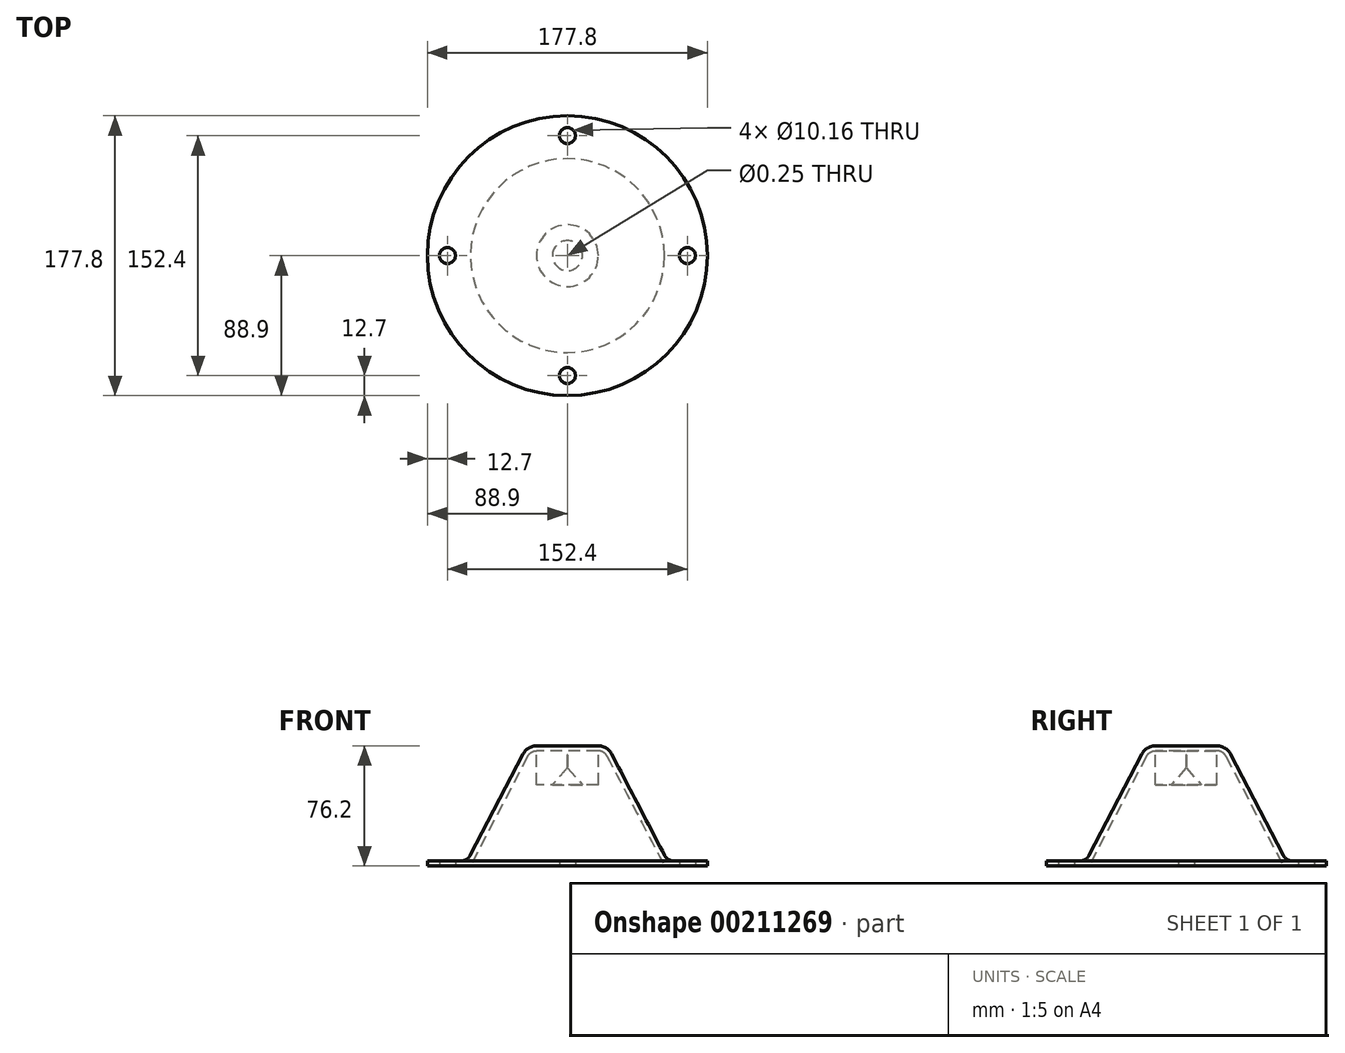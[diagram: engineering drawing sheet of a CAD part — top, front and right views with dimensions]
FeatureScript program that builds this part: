
annotation { "Feature Type Name" : "Feature", "Feature Type Description" : "" }
export const myFeature = defineFeature(function(context is Context, id is Id, definition is map)
    precondition{}
    {
        {
            var Q0;
            Q0=qCreatedBy(makeId("Front.planeOp"),FACE);
            var sketch = newSketch(context, id + "F0", { "sketchPlane" : qUnion([Q0])});
            skLineSegment(sketch, "E0", {"start": v(61.58, 0) * mm, "end": v(88.9, 0) * mm});
            skLineSegment(sketch, "E1", {"start": v(0, 73.03) * mm, "end": v(0, 76.2) * mm});
            skLineSegment(sketch, "E2", {"start": v(88.9, 0) * mm, "end": v(88.9, 3.18) * mm});
            skLineSegment(sketch, "E3", {"start": v(88.9, 3.18) * mm, "end": v(67.35, 3.18) * mm});
            skLineSegment(sketch, "E4", {"start": v(0, 76.2) * mm, "end": v(19.63, 76.2) * mm});
            skLineSegment(sketch, "E5", {"start": v(28.07, 71.08) * mm, "end": v(61.72, 6.59) * mm});
            skLineSegment(sketch, "E6", {"start": v(0, 76.2) * mm, "end": v(0, 73.03) * mm});
            skLineSegment(sketch, "E7", {"start": v(0, 73.03) * mm, "end": v(19.63, 73.03) * mm});
            skLineSegment(sketch, "E8", {"start": v(25.26, 69.61) * mm, "end": v(61.58, 0) * mm});
            skPoint(sketch, "E9.orphan", {"position": v(-148.64, 0) * mm});
            skPoint(sketch, "E10.visualSharp", {"position": v(23.48, 73.03) * mm});
            skArc(sketch, "E10.filletArc", {"start": v(25.26, 69.61) * mm, "mid": v(22.92, 72.1) * mm, "end": v(19.63, 73.03) * mm});
            skPoint(sketch, "E11.visualSharp", {"position": v(63.5, 3.18) * mm});
            skArc(sketch, "E11.filletArc", {"start": v(61.72, 6.59) * mm, "mid": v(64.06, 4.1) * mm, "end": v(67.35, 3.18) * mm});
            skPoint(sketch, "E12.visualSharp", {"position": v(25.4, 76.2) * mm});
            skArc(sketch, "E12.filletArc", {"start": v(28.07, 71.08) * mm, "mid": v(24.56, 74.82) * mm, "end": v(19.63, 76.2) * mm});
            skLineSegment(sketch, "E13", {"start": v(0, 54.17) * mm, "end": v(0, 16.24) * mm});
            skSolve(sketch);
        }
        {
            var Q0;
            Q0 = qSketchRegion(id + "F0", true);
            var Q1;
            Q1=sQuery(id+"F0.wireOp",EDGE,"E13");
            revolve(context, id + "F1", {"entities" : qUnion([Q0]), "axis" : qUnion([Q1]), "revolveType" : RevolveType.FULL});
        }
        {
            var Q0;
            Q0=makeQuery(id+"F1.opRevolve","SWEPT_FACE",FACE,{"disambiguationData":[OSD([sQuery(id+"F0.wireOp",EDGE,"E0")])]});
            var sketch = newSketch(context, id + "F2", { "sketchPlane" : qUnion([Q0])});
            skCircle(sketch, "E14", {"center": v(0, 76.2) * mm, "radius": 5.08 * mm});
            skCircle(sketch, "E15.1.0", {"center": v(-76.2, 0) * mm, "radius": 5.08 * mm});
            skCircle(sketch, "E15.2.0", {"center": v(0, -76.2) * mm, "radius": 5.08 * mm});
            skCircle(sketch, "E15.3.0", {"center": v(76.2, 0) * mm, "radius": 5.08 * mm});
            skPoint(sketch, "E15.center", {"position": v(0, 0) * mm});
            skSolve(sketch);
        }
        {
            var Q0;
            Q0 = qSketchRegion(id + "F2", true);
            extrude(context, id + "F3", {"entities" : qUnion([Q0]), "operationType" : NewBodyOperationType.REMOVE, "oppositeDirection" : true, "depth" : 25.4 * mm});
        }
        {
            var Q0;
            Q0=makeQuery(id+"F1.opRevolve","SWEPT_FACE",FACE,{"disambiguationData":[OSD([sQuery(id+"F0.wireOp",EDGE,"E7")])]});
            var sketch = newSketch(context, id + "F4", { "sketchPlane" : qUnion([Q0])});
            skSolve(sketch);
        }
        {
            var Q0;
            Q0 = qSketchRegion(id + "F4", true);
            var Q1;
            Q1=makeQuery(id+"F4.imprint","IMPRINT",FACE,{"disambiguationData":[TD([[makeQuery(id+"F4.imprint","IMPRINT",EDGE,{"derivedFrom":makeQuery(id+"F1.opRevolve","SWEPT_EDGE",EDGE,{"disambiguationData":[OSD([sQuery(id+"F0.wireOp",EDGE,"E7"),sQuery(id+"F0.wireOp",EDGE,"E10.filletArc")])]})}),-1.0]])]});
            extrude(context, id + "F5", {"entities" : qUnion([Q0, Q1]), "operationType" : NewBodyOperationType.ADD, "depth" : 21.59 * mm});
        }
        {
            var Q0;
            Q0=makeQuery(id+"F5.opExtrude","CAP_FACE",FACE,{"disambiguationData":[OSD([sQuery(id+"F0.wireOp",EDGE,"E7"),sQuery(id+"F0.wireOp",EDGE,"E10.filletArc")])],"isStart":false});
            var sketch = newSketch(context, id + "F6", { "sketchPlane" : qUnion([Q0])});
            skPoint(sketch, "E16", {"position": v(0, 0) * mm});
            skSolve(sketch);
        }
        {
            var Q0;
            Q0=sQuery(id+"F6.wireOp",VERTEX,"E16");
            var Q1;
            Q1=makeQuery(id+"F1.opRevolve","SWEPT_BODY",BODY,{"disambiguationData":[OSD([sQuery(id+"F0.wireOp",EDGE,"E0"),sQuery(id+"F0.wireOp",EDGE,"E2"),sQuery(id+"F0.wireOp",EDGE,"E3"),sQuery(id+"F0.wireOp",EDGE,"E4"),sQuery(id+"F0.wireOp",EDGE,"E5"),sQuery(id+"F0.wireOp",EDGE,"E6"),sQuery(id+"F0.wireOp",EDGE,"E7"),sQuery(id+"F0.wireOp",EDGE,"E8"),sQuery(id+"F0.wireOp",EDGE,"E10.filletArc"),sQuery(id+"F0.wireOp",EDGE,"E11.filletArc"),sQuery(id+"F0.wireOp",EDGE,"E12.filletArc")])]});
            hole(context, id + "F7", {"style" : HoleStyle.C_SINK, "endStyle" : HoleEndStyle.BLIND, "holeDiameter" : 0.25 * mm, "cSinkDiameter" : 19.05 * mm, "cSinkAngle" : 82 * degree, "holeDepth" : 19.05 * mm, "startFromSketch" : true, "locations" : qUnion([Q0]), "scope" : qUnion([Q1])});
        }
    });
